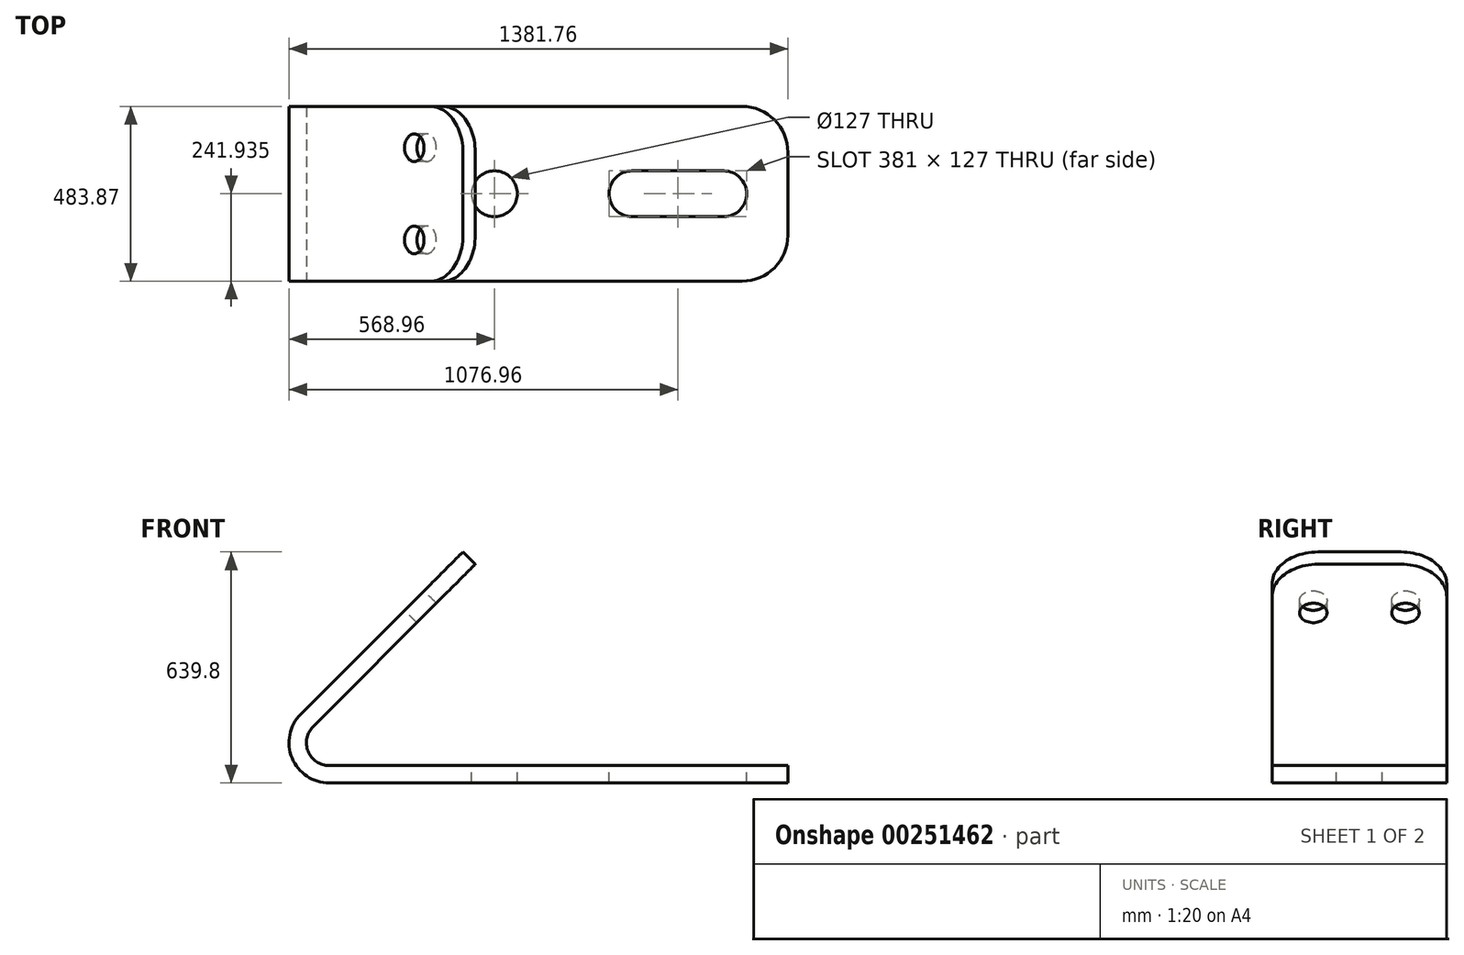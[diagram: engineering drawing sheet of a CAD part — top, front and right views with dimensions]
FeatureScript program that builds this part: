
annotation { "Feature Type Name" : "Feature", "Feature Type Description" : "" }
export const myFeature = defineFeature(function(context is Context, id is Id, definition is map)
    precondition{}
    {
        {
            var Q0;
            Q0=qCreatedBy(makeId("Front.planeOp"),FACE);
            var sketch = newSketch(context, id + "F0", { "sketchPlane" : qUnion([Q0])});
            skLineSegment(sketch, "E0", {"start": v(0, 0) * mm, "end": v(1270, 0) * mm});
            skLineSegment(sketch, "E1", {"start": v(-79.03, 190.79) * mm, "end": v(369.99, 639.8) * mm});
            skArc(sketch, "E2", {"start": v(-79.03, 190.79) * mm, "mid": v(-103.25, 69) * mm, "end": v(0, 0) * mm});
            skLineSegment(sketch, "E3", {"start": v(1270, 0) * mm, "end": v(1270, 48.26) * mm});
            skLineSegment(sketch, "E4", {"start": v(1270, 48.26) * mm, "end": v(0, 48.26) * mm});
            skLineSegment(sketch, "E5", {"start": v(369.99, 639.8) * mm, "end": v(404.11, 605.67) * mm});
            skLineSegment(sketch, "E6", {"start": v(404.11, 605.67) * mm, "end": v(-44.9, 156.66) * mm});
            skArc(sketch, "E7", {"start": v(-44.9, 156.66) * mm, "mid": v(-58.67, 87.46) * mm, "end": v(0, 48.26) * mm});
            skSolve(sketch);
        }
        {
            var Q0;
            Q0=makeQuery(id+"F0.imprint","IMPRINT",FACE,{"disambiguationData":[TD([[makeQuery(id+"F0.imprint","IMPRINT",EDGE,{"derivedFrom":sQuery(id+"F0.wireOp",EDGE,"E0")}),1.0]])]});
            extrude(context, id + "F1", {"entities" : qUnion([Q0]), "oppositeDirection" : true, "depth" : 483.87 * mm});
        }
        {
            var Q0;
            Q0=makeQuery(id+"F1.opExtrude","SWEPT_FACE",FACE,{"disambiguationData":[OSD([sQuery(id+"F0.wireOp",EDGE,"E1")])]});
            var sketch = newSketch(context, id + "F2", { "sketchPlane" : qUnion([Q0])});
            skCircle(sketch, "E8", {"center": v(-369.57, 523.53) * mm, "radius": 38.1 * mm});
            skCircle(sketch, "E9", {"center": v(-114.3, 523.53) * mm, "radius": 38.1 * mm});
            skSolve(sketch);
        }
        {
            var Q0;
            Q0=makeQuery(id+"F2.imprint","IMPRINT",FACE,{"disambiguationData":[TD([[makeQuery(id+"F2.imprint","IMPRINT",EDGE,{"derivedFrom":sQuery(id+"F2.wireOp",EDGE,"E8")}),1.0]])]});
            var Q1;
            Q1=makeQuery(id+"F2.imprint","IMPRINT",FACE,{"disambiguationData":[TD([[makeQuery(id+"F2.imprint","IMPRINT",EDGE,{"derivedFrom":sQuery(id+"F2.wireOp",EDGE,"E9")}),1.0]])]});
            extrude(context, id + "F3", {"entities" : qUnion([Q0, Q1]), "operationType" : NewBodyOperationType.REMOVE, "oppositeDirection" : true, "depth" : 76.2 * mm});
        }
        {
            var Q0;
            Q0=makeQuery(id+"F1.opExtrude","CAP_EDGE",EDGE,{"disambiguationData":[OSD([sQuery(id+"F0.wireOp",EDGE,"E5")])],"isStart":false});
            var Q1;
            Q1=makeQuery(id+"F1.opExtrude","CAP_EDGE",EDGE,{"disambiguationData":[OSD([sQuery(id+"F0.wireOp",EDGE,"E5")])],"isStart":true});
            fillet(context, id + "F4", {"entities" : qUnion([Q0, Q1]), "radius" : 127 * mm, "tangentPropagation" : true, "allowEdgeOverflow" : false});
        }
        {
            var Q0;
            Q0=makeQuery(id+"F1.opExtrude","SWEPT_FACE",FACE,{"disambiguationData":[OSD([sQuery(id+"F0.wireOp",EDGE,"E4")])]});
            var sketch = newSketch(context, id + "F5", { "sketchPlane" : qUnion([Q0])});
            skLineSegment(sketch, "E10", {"start": v(1270, 241.94) * mm, "end": v(457.2, 241.94) * mm, "construction": true});
            skPoint(sketch, "E10.endSnap0", {"position": v(1270, 241.94) * mm});
            skCircle(sketch, "E11", {"center": v(457.2, 241.94) * mm, "radius": 63.5 * mm});
            skSolve(sketch);
        }
        {
            var Q0;
            Q0=makeQuery(id+"F5.imprint","IMPRINT",FACE,{"disambiguationData":[TD([[makeQuery(id+"F5.imprint","IMPRINT",EDGE,{"derivedFrom":sQuery(id+"F5.wireOp",EDGE,"E11")}),1.0]])]});
            extrude(context, id + "F6", {"entities" : qUnion([Q0]), "operationType" : NewBodyOperationType.REMOVE, "endBound" : BoundingType.THROUGH_ALL, "oppositeDirection" : true, "depth" : 25.4 * mm});
        }
        {
            var Q0;
            Q0=makeQuery(id+"F1.opExtrude","SWEPT_FACE",FACE,{"disambiguationData":[OSD([sQuery(id+"F0.wireOp",EDGE,"E4")])]});
            var sketch = newSketch(context, id + "F7", { "sketchPlane" : qUnion([Q0])});
            skLineSegment(sketch, "E12", {"start": v(1270, 241.94) * mm, "end": v(1155.7, 241.94) * mm, "construction": true});
            skPoint(sketch, "E12.endSnap0", {"position": v(1270, 241.94) * mm});
            skLineSegment(sketch, "E13", {"start": v(1155.7, 241.94) * mm, "end": v(774.7, 241.94) * mm, "construction": true});
            skLineSegment(sketch, "E14.bottom", {"start": v(1155.7, 305.44) * mm, "end": v(774.7, 305.44) * mm});
            skLineSegment(sketch, "E14.top", {"start": v(1155.7, 178.44) * mm, "end": v(774.7, 178.44) * mm});
            skLineSegment(sketch, "E14.left", {"start": v(1155.7, 305.44) * mm, "end": v(1155.7, 178.44) * mm});
            skLineSegment(sketch, "E14.right", {"start": v(774.7, 305.44) * mm, "end": v(774.7, 178.44) * mm});
            skPoint(sketch, "E14.middle", {"position": v(965.2, 241.94) * mm});
            skLineSegment(sketch, "E15", {"start": v(774.7, 241.94) * mm, "end": v(838.2, 241.94) * mm});
            skLineSegment(sketch, "E16", {"start": v(1155.7, 241.94) * mm, "end": v(1092.2, 241.94) * mm});
            skCircle(sketch, "E17", {"center": v(838.2, 241.94) * mm, "radius": 63.5 * mm});
            skCircle(sketch, "E18", {"center": v(1092.2, 241.94) * mm, "radius": 63.5 * mm});
            skSolve(sketch);
        }
        {
            var Q0;
            {var subQ0=sQuery(id+"F7.wireOp",EDGE,"E17");var subQ1=makeQuery(id+"F7.imprint","INTERSECT",VERTEX,{"derivedFrom":[sQuery(id+"F7.wireOp",EDGE,"E14.right"),subQ0]});Q0=makeQuery(id+"F7.imprint","IMPRINT",FACE,{"disambiguationData":[TD([[makeQuery(id+"F7.imprint","IMPRINT",EDGE,{"disambiguationData":[TD([[subQ1,1.0]])],"derivedFrom":subQ0}),1.0]])]});}
            var Q1;
            {var subQ0=sQuery(id+"F7.wireOp",EDGE,"E18");var subQ1=sQuery(id+"F7.wireOp",EDGE,"E14.bottom");var subQ2=makeQuery(id+"F7.imprint","INTERSECT",VERTEX,{"derivedFrom":[subQ1,subQ0]});Q1=makeQuery(id+"F7.imprint","IMPRINT",FACE,{"disambiguationData":[TD([[makeQuery(id+"F7.imprint","IMPRINT",EDGE,{"disambiguationData":[TD([[subQ2,-1.0]])],"derivedFrom":subQ1}),1.0]])]});}
            var Q2;
            {var subQ0=sQuery(id+"F7.wireOp",EDGE,"E18");var subQ1=makeQuery(id+"F7.imprint","INTERSECT",VERTEX,{"derivedFrom":[sQuery(id+"F7.wireOp",EDGE,"E14.left"),subQ0]});Q2=makeQuery(id+"F7.imprint","IMPRINT",FACE,{"disambiguationData":[TD([[makeQuery(id+"F7.imprint","IMPRINT",EDGE,{"disambiguationData":[TD([[subQ1,-1.0]])],"derivedFrom":subQ0}),1.0]])]});}
            extrude(context, id + "F8", {"entities" : qUnion([Q0, Q1, Q2]), "operationType" : NewBodyOperationType.REMOVE, "endBound" : BoundingType.THROUGH_ALL, "oppositeDirection" : true, "depth" : 25.4 * mm});
        }
        {
            var Q0;
            Q0=makeQuery(id+"F1.opExtrude","CAP_EDGE",EDGE,{"disambiguationData":[OSD([sQuery(id+"F0.wireOp",EDGE,"E3")])],"isStart":false});
            var Q1;
            Q1=makeQuery(id+"F1.opExtrude","CAP_EDGE",EDGE,{"disambiguationData":[OSD([sQuery(id+"F0.wireOp",EDGE,"E3")])],"isStart":true});
            fillet(context, id + "F9", {"entities" : qUnion([Q0, Q1]), "radius" : 127 * mm, "tangentPropagation" : true, "allowEdgeOverflow" : false});
        }
    });
